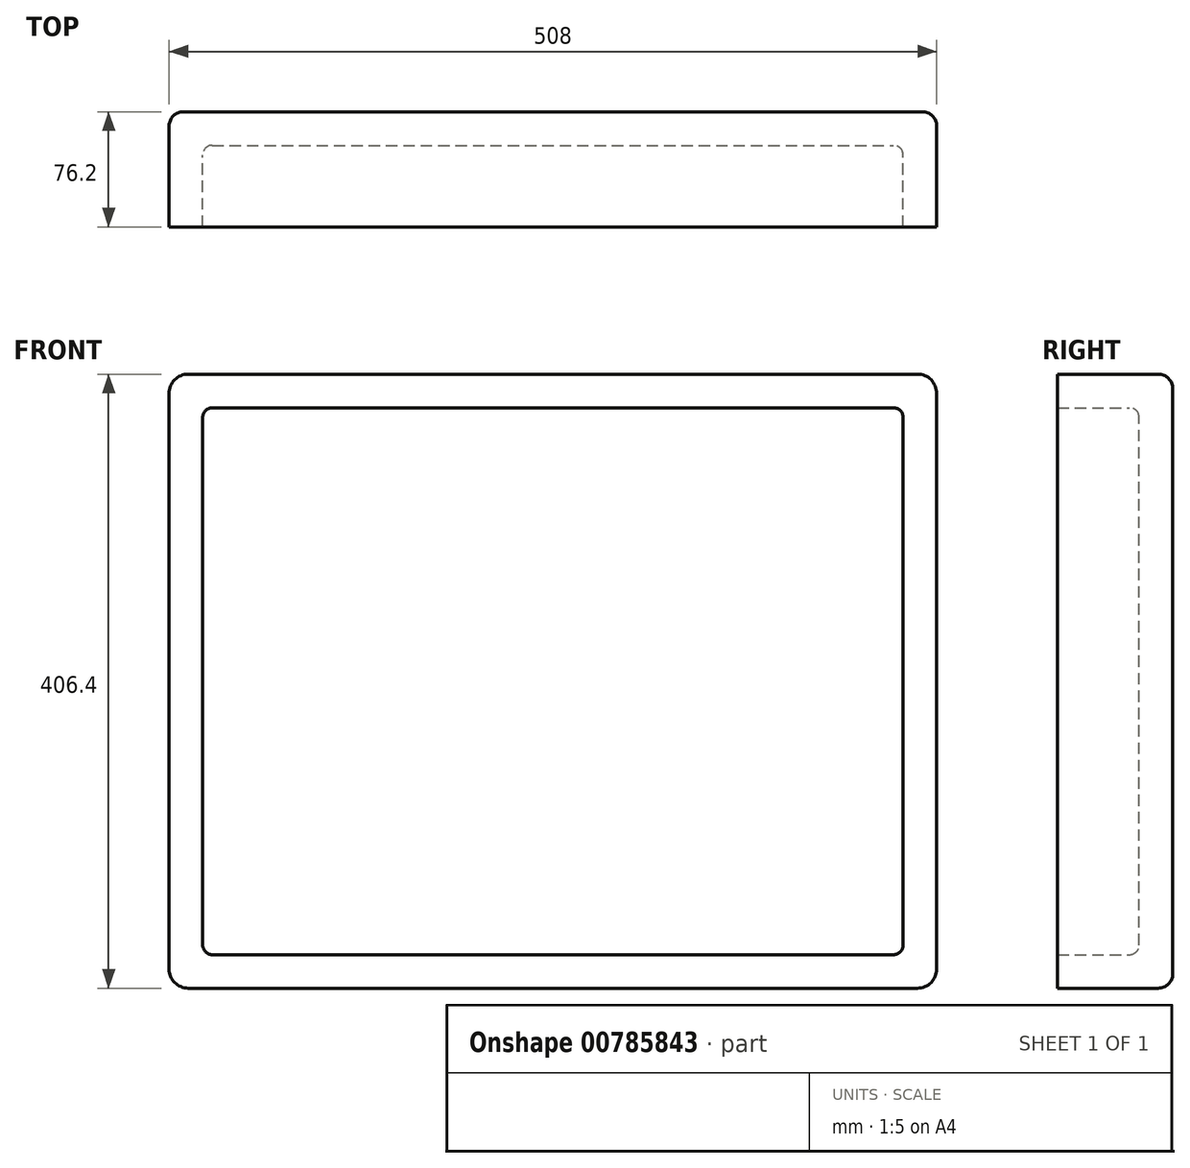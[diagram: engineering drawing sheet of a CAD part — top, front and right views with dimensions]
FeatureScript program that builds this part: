
annotation { "Feature Type Name" : "Feature", "Feature Type Description" : "" }
export const myFeature = defineFeature(function(context is Context, id is Id, definition is map)
    precondition{}
    {
        {
            var Q0;
            Q0=qCreatedBy(makeId("Front.planeOp"),FACE);
            var sketch = newSketch(context, id + "F0", { "sketchPlane" : qUnion([Q0])});
            skLineSegment(sketch, "E0.bottom", {"start": v(12.7, 0) * mm, "end": v(495.3, 0) * mm});
            skLineSegment(sketch, "E0.top", {"start": v(12.7, 406.4) * mm, "end": v(495.3, 406.4) * mm});
            skLineSegment(sketch, "E0.left", {"start": v(0, 12.7) * mm, "end": v(0, 393.7) * mm});
            skLineSegment(sketch, "E0.right", {"start": v(508, 12.7) * mm, "end": v(508, 393.7) * mm});
            skPoint(sketch, "E1.visualSharp", {"position": v(0, 0) * mm});
            skArc(sketch, "E1.filletArc", {"start": v(0, 12.7) * mm, "mid": v(3.72, 3.72) * mm, "end": v(12.7, 0) * mm});
            skPoint(sketch, "E2.visualSharp", {"position": v(508, 0) * mm});
            skArc(sketch, "E2.filletArc", {"start": v(495.3, 0) * mm, "mid": v(504.28, 3.72) * mm, "end": v(508, 12.7) * mm});
            skPoint(sketch, "E3.visualSharp", {"position": v(508, 406.4) * mm});
            skArc(sketch, "E3.filletArc", {"start": v(508, 393.7) * mm, "mid": v(504.28, 402.68) * mm, "end": v(495.3, 406.4) * mm});
            skPoint(sketch, "E4.visualSharp", {"position": v(0, 406.4) * mm});
            skArc(sketch, "E4.filletArc", {"start": v(12.7, 406.4) * mm, "mid": v(3.72, 402.68) * mm, "end": v(0, 393.7) * mm});
            skSolve(sketch);
        }
        {
            var Q0;
            Q0=makeQuery(id+"F0.imprint","IMPRINT",FACE,{"disambiguationData":[TD([[makeQuery(id+"F0.imprint","IMPRINT",EDGE,{"derivedFrom":sQuery(id+"F0.wireOp",EDGE,"E0.bottom")}),1.0]])]});
            extrude(context, id + "F1", {"entities" : qUnion([Q0]), "depth" : 76.2 * mm, "offsetDistance" : 25.4 * mm});
        }
        {
            var Q0;
            Q0=makeQuery(id+"F1.opExtrude","CAP_FACE",FACE,{"disambiguationData":[OSD([sQuery(id+"F0.wireOp",EDGE,"E0.bottom"),sQuery(id+"F0.wireOp",EDGE,"E0.top"),sQuery(id+"F0.wireOp",EDGE,"E0.left"),sQuery(id+"F0.wireOp",EDGE,"E0.right"),sQuery(id+"F0.wireOp",EDGE,"E1.filletArc"),sQuery(id+"F0.wireOp",EDGE,"E2.filletArc"),sQuery(id+"F0.wireOp",EDGE,"E3.filletArc"),sQuery(id+"F0.wireOp",EDGE,"E4.filletArc")])],"isStart":false});
            shell(context, id + "F2", {"entities" : qUnion([Q0]), "thickness" : 22.22 * mm});
        }
        {
            var Q0;
            Q0=makeQuery(id+"F1.opExtrude","CAP_EDGE",EDGE,{"disambiguationData":[OSD([sQuery(id+"F0.wireOp",EDGE,"E0.top")])],"isStart":true});
            fillet(context, id + "F3", {"entities" : qUnion([Q0]), "radius" : 9.52 * mm, "tangentPropagation" : true, "allowEdgeOverflow" : false});
        }
        {
            var Q0;
            Q0=makeQuery(id+"F2.opShell","OFFSET_EDGE",EDGE,{"disambiguationData":[OSD([sQuery(id+"F0.wireOp",EDGE,"E0.bottom"),sQuery(id+"F0.wireOp",EDGE,"E0.left"),sQuery(id+"F0.wireOp",EDGE,"E1.filletArc")])]});
            var Q1;
            Q1=makeQuery(id+"F2.opShell","OFFSET_EDGE",EDGE,{"disambiguationData":[OSD([sQuery(id+"F0.wireOp",EDGE,"E0.bottom"),sQuery(id+"F0.wireOp",EDGE,"E0.right"),sQuery(id+"F0.wireOp",EDGE,"E2.filletArc")])]});
            var Q2;
            Q2=makeQuery(id+"F2.opShell","OFFSET_EDGE",EDGE,{"disambiguationData":[OSD([sQuery(id+"F0.wireOp",EDGE,"E0.top"),sQuery(id+"F0.wireOp",EDGE,"E0.right"),sQuery(id+"F0.wireOp",EDGE,"E3.filletArc")])]});
            var Q3;
            Q3=makeQuery(id+"F2.opShell","OFFSET_EDGE",EDGE,{"disambiguationData":[OSD([sQuery(id+"F0.wireOp",EDGE,"E0.top"),sQuery(id+"F0.wireOp",EDGE,"E0.left"),sQuery(id+"F0.wireOp",EDGE,"E4.filletArc")])]});
            fillet(context, id + "F4", {"entities" : qUnion([Q0, Q1, Q2, Q3]), "radius" : 6.35 * mm, "tangentPropagation" : true, "allowEdgeOverflow" : false});
        }
        {
            var Q0;
            {var subQ0=sQuery(id+"F0.wireOp",EDGE,"E0.left");Q0=makeQuery(id+"F2.opShell","OFFSET_EDGE",EDGE,{"disambiguationData":[OSD([subQ0]),TDD([makeQuery(id+"F1.opExtrude","CAP_EDGE",EDGE,{"disambiguationData":[OSD([subQ0])],"isStart":true})])]});}
            fillet(context, id + "F5", {"entities" : qUnion([Q0]), "radius" : 6.35 * mm, "tangentPropagation" : true, "allowEdgeOverflow" : false});
        }
    });
